# Revit family: QF_BOURGEAT_2GN_bain_marie mobile_sans_etuve_cuve_separees
name_source: partatom
category: Equipement spécialisé
revit_build: Autodesk Revit 2015 (Build: 20140606_1530(x64)
units: mm (PartAtom-declared; Revit-internal decimal feet)

## types (2) — shared parameters
Charge max = 60.00 kg
Diamètre de Raccordement Evacuation = 27 mm
Fabricant = BOURGEAT
Fréquence = 50 Hz
Hauteur hors tout = 900 mm  [stored 2.95276 ft]
Indice de protection = 21
Intensité nominale = 6 A
Nature_isolant = 30mm laine de roche
Phase = 2
Spécification du Fabricant = bain-marie mobiles
Tension = 230 V
URL catalogue = http://www.bourgeat.fr

## per-type parameters (varying)
| type | Longueur hors tout | Modèle | Poids net à vide | Profondeur hors tout | Puissance électrique  | commande_grand_cote | commande_petit_cote | lg_barre_transport |
| commandes_petit_cote | 900 mm  [stored 2.95276 ft] | 872012 | 45.00 kg | 690 mm  [stored 2.26378 ft] | 1400 W | Non | Oui | 635 mm |
| commande_grand_cote | 835 mm | 872312 | 40.00 kg | 755 mm  [stored 2.47703 ft] | 1300 W | Oui | Non | 566 mm  [stored 1.85696 ft] |

note: [stored X ft] marks values corroborated as IEEE doubles in the binary element streams (Revit-internal decimal feet)
